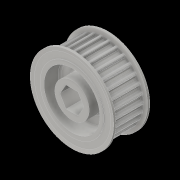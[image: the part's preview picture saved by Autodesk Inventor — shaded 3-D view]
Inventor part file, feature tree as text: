
AUTODESK INVENTOR PART (.ipt)
format: ipt  version: 2016 (Build 200138000, 138)  size: 1,234,944 bytes
history: native  units: in
note: dims shown in document units (in); Inventor stores cm internally (conversion verified against a paired STEP export)
features: mirror x1
ambient origin geometry x8: Origin, YZ Plane, XZ Plane, XY Plane, X Axis, Y Axis, Z Axis, Center Point
bodies: Solid1 (feature_tree)
feature tree (1):
  mirror  "Mirror1"
